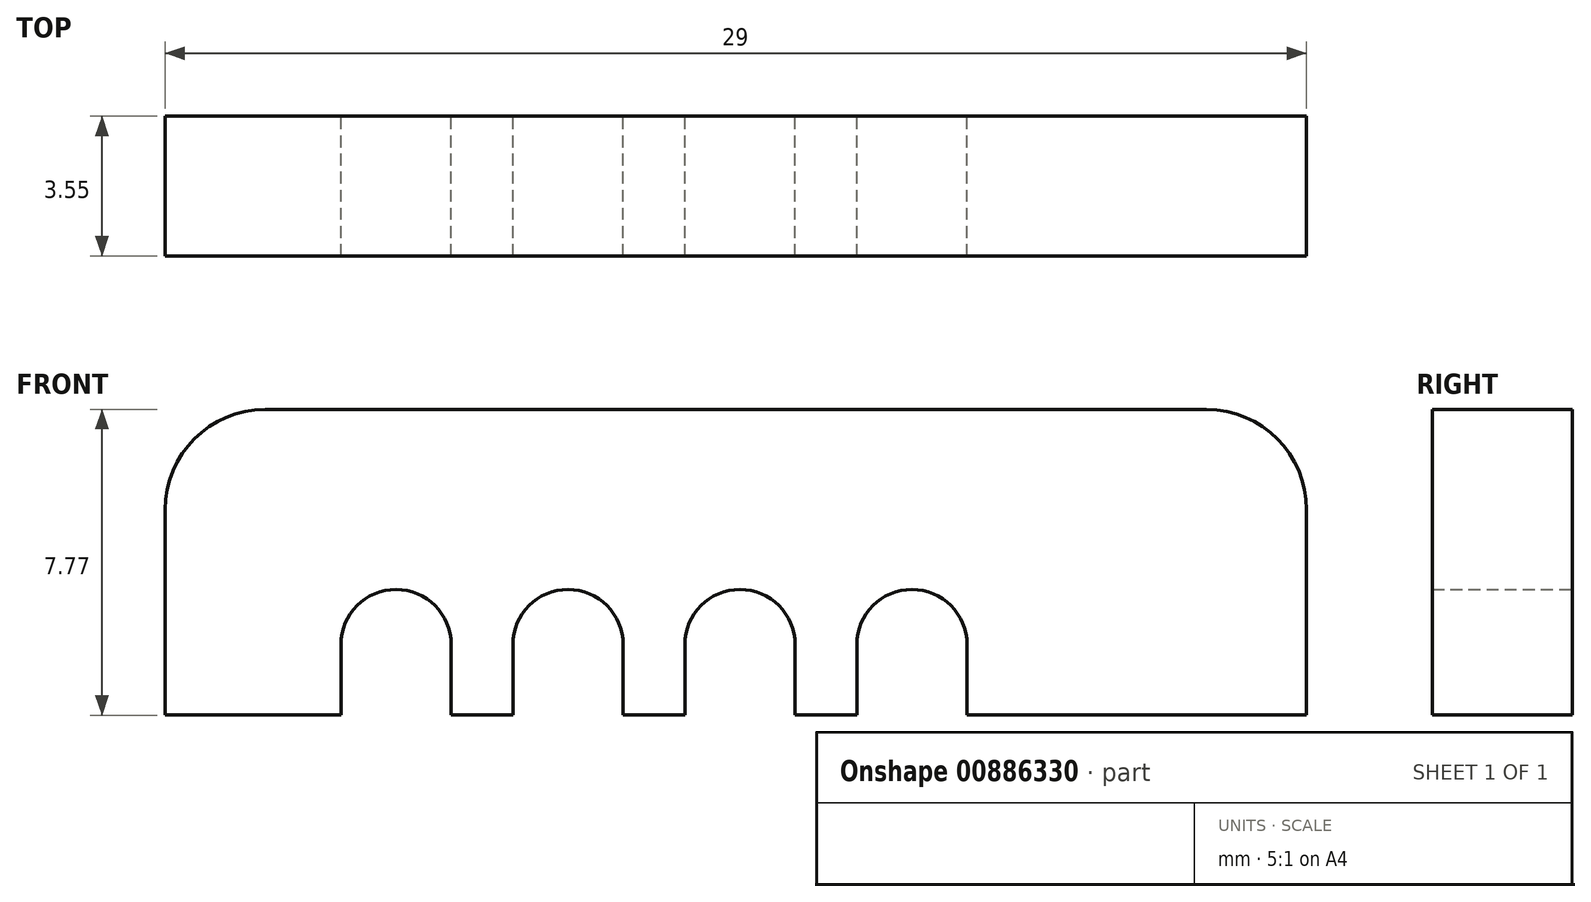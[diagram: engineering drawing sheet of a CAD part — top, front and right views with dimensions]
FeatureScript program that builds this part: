
annotation { "Feature Type Name" : "Feature", "Feature Type Description" : "" }
export const myFeature = defineFeature(function(context is Context, id is Id, definition is map)
    precondition{}
    {
        {
            var Q0;
            Q0=qCreatedBy(makeId("Front.planeOp"),FACE);
            var sketch = newSketch(context, id + "F0", { "sketchPlane" : qUnion([Q0])});
            skLineSegment(sketch, "E0.bottom", {"start": v(-13.53, 11.75) * mm, "end": v(15.47, 11.75) * mm});
            skLineSegment(sketch, "E0.top", {"start": v(-13.53, -11.75) * mm, "end": v(15.47, -11.75) * mm});
            skLineSegment(sketch, "E0.left", {"start": v(-13.53, 11.75) * mm, "end": v(-13.53, -11.75) * mm});
            skLineSegment(sketch, "E0.right", {"start": v(15.47, 11.75) * mm, "end": v(15.47, -11.75) * mm});
            skArc(sketch, "E1", {"start": v(-10.99, 11.75) * mm, "mid": v(-12.78, 11) * mm, "end": v(-13.53, 9.2) * mm});
            skArc(sketch, "E2", {"start": v(15.47, 9.2) * mm, "mid": v(14.73, 11) * mm, "end": v(12.93, 11.75) * mm});
            skArc(sketch, "E3", {"start": v(-13.53, -9.2) * mm, "mid": v(-12.78, -11) * mm, "end": v(-10.99, -11.75) * mm});
            skArc(sketch, "E4", {"start": v(12.93, -11.75) * mm, "mid": v(14.73, -11) * mm, "end": v(15.47, -9.2) * mm});
            skCircle(sketch, "E5", {"center": v(-7.66, 5.78) * mm, "radius": 1.4 * mm});
            skCircle(sketch, "E6", {"center": v(-3.29, 5.78) * mm, "radius": 1.4 * mm});
            skCircle(sketch, "E7", {"center": v(1.08, 5.78) * mm, "radius": 1.4 * mm});
            skCircle(sketch, "E8", {"center": v(5.45, 5.78) * mm, "radius": 1.4 * mm});
            skCircle(sketch, "E9", {"center": v(-5.47, 1.8) * mm, "radius": 1.4 * mm});
            skCircle(sketch, "E10", {"center": v(-1.1, 1.8) * mm, "radius": 1.4 * mm});
            skCircle(sketch, "E11", {"center": v(3.26, 1.8) * mm, "radius": 1.4 * mm});
            skCircle(sketch, "E12", {"center": v(7.63, 1.8) * mm, "radius": 1.4 * mm});
            skLineSegment(sketch, "E13.bottom", {"start": v(-14.03, 12.38) * mm, "end": v(20.56, 12.38) * mm});
            skLineSegment(sketch, "E13.top", {"start": v(-14.03, -12.38) * mm, "end": v(20.56, -12.38) * mm});
            skLineSegment(sketch, "E13.left", {"start": v(-14.03, 12.38) * mm, "end": v(-14.03, -12.38) * mm});
            skLineSegment(sketch, "E13.right", {"start": v(20.56, 12.38) * mm, "end": v(20.56, -12.38) * mm});
            skCircle(sketch, "E14", {"center": v(17.78, 0) * mm, "radius": 1.9 * mm});
            skArc(sketch, "E15", {"start": v(20.56, 9.2) * mm, "mid": v(19.63, 11.45) * mm, "end": v(17.39, 12.38) * mm});
            skArc(sketch, "E16", {"start": v(17.39, -12.38) * mm, "mid": v(19.63, -11.45) * mm, "end": v(20.56, -9.2) * mm});
            skArc(sketch, "E17", {"start": v(-14.03, -9.2) * mm, "mid": v(-13.1, -11.45) * mm, "end": v(-10.86, -12.38) * mm});
            skArc(sketch, "E18", {"start": v(-10.86, 12.38) * mm, "mid": v(-13.1, 11.45) * mm, "end": v(-14.03, 9.2) * mm});
            skLineSegment(sketch, "E19", {"start": v(-13.53, 3.98) * mm, "end": v(15.47, 3.98) * mm});
            skLineSegment(sketch, "E20", {"start": v(-13.53, 3.58) * mm, "end": v(15.47, 3.58) * mm});
            skLineSegment(sketch, "E21.bottom", {"start": v(-9.06, 5.78) * mm, "end": v(-6.26, 5.78) * mm});
            skLineSegment(sketch, "E21.top", {"start": v(-9.06, 3.98) * mm, "end": v(-6.26, 3.98) * mm});
            skLineSegment(sketch, "E21.left", {"start": v(-9.06, 5.78) * mm, "end": v(-9.06, 3.98) * mm});
            skLineSegment(sketch, "E21.right", {"start": v(-6.26, 5.78) * mm, "end": v(-6.26, 3.98) * mm});
            skLineSegment(sketch, "E22.bottom", {"start": v(-4.69, 5.78) * mm, "end": v(-1.89, 5.78) * mm});
            skLineSegment(sketch, "E22.top", {"start": v(-4.69, 3.98) * mm, "end": v(-1.89, 3.98) * mm});
            skLineSegment(sketch, "E22.left", {"start": v(-4.69, 5.78) * mm, "end": v(-4.69, 3.98) * mm});
            skLineSegment(sketch, "E22.right", {"start": v(-1.89, 5.78) * mm, "end": v(-1.89, 3.98) * mm});
            skLineSegment(sketch, "E23.bottom", {"start": v(-0.32, 5.78) * mm, "end": v(2.48, 5.78) * mm});
            skLineSegment(sketch, "E23.top", {"start": v(-0.32, 3.98) * mm, "end": v(2.48, 3.98) * mm});
            skLineSegment(sketch, "E23.left", {"start": v(-0.32, 5.78) * mm, "end": v(-0.32, 3.98) * mm});
            skLineSegment(sketch, "E23.right", {"start": v(2.48, 5.78) * mm, "end": v(2.48, 3.98) * mm});
            skLineSegment(sketch, "E24.bottom", {"start": v(4.05, 5.78) * mm, "end": v(6.85, 5.78) * mm});
            skLineSegment(sketch, "E24.top", {"start": v(4.05, 3.98) * mm, "end": v(6.85, 3.98) * mm});
            skLineSegment(sketch, "E24.left", {"start": v(4.05, 5.78) * mm, "end": v(4.05, 3.98) * mm});
            skLineSegment(sketch, "E24.right", {"start": v(6.85, 5.78) * mm, "end": v(6.85, 3.98) * mm});
            skLineSegment(sketch, "E25.bottom", {"start": v(-6.87, 3.58) * mm, "end": v(-4.07, 3.58) * mm});
            skLineSegment(sketch, "E25.top", {"start": v(-6.87, 1.8) * mm, "end": v(-4.07, 1.8) * mm});
            skLineSegment(sketch, "E25.left", {"start": v(-6.87, 3.58) * mm, "end": v(-6.87, 1.8) * mm});
            skLineSegment(sketch, "E25.right", {"start": v(-4.07, 3.58) * mm, "end": v(-4.07, 1.8) * mm});
            skLineSegment(sketch, "E26.bottom", {"start": v(-2.5, 3.58) * mm, "end": v(0.3, 3.58) * mm});
            skLineSegment(sketch, "E26.top", {"start": v(-2.5, 1.8) * mm, "end": v(0.3, 1.8) * mm});
            skLineSegment(sketch, "E26.left", {"start": v(-2.5, 3.58) * mm, "end": v(-2.5, 1.8) * mm});
            skLineSegment(sketch, "E26.right", {"start": v(0.3, 3.58) * mm, "end": v(0.3, 1.8) * mm});
            skLineSegment(sketch, "E27.bottom", {"start": v(1.86, 3.58) * mm, "end": v(4.66, 3.58) * mm});
            skLineSegment(sketch, "E27.top", {"start": v(1.86, 1.8) * mm, "end": v(4.66, 1.8) * mm});
            skLineSegment(sketch, "E27.left", {"start": v(1.86, 3.58) * mm, "end": v(1.86, 1.8) * mm});
            skLineSegment(sketch, "E27.right", {"start": v(4.66, 3.58) * mm, "end": v(4.66, 1.8) * mm});
            skLineSegment(sketch, "E28.bottom", {"start": v(6.23, 3.58) * mm, "end": v(9.03, 3.58) * mm});
            skLineSegment(sketch, "E28.top", {"start": v(6.23, 1.8) * mm, "end": v(9.03, 1.8) * mm});
            skLineSegment(sketch, "E28.left", {"start": v(6.23, 3.58) * mm, "end": v(6.23, 1.8) * mm});
            skLineSegment(sketch, "E28.right", {"start": v(9.03, 3.58) * mm, "end": v(9.03, 1.8) * mm});
            skSolve(sketch);
        }
        {
            var Q0;
            {var subQ21=sQuery(id+"F0.wireOp",EDGE,"E1");Q0=makeQuery(id+"F0.imprint","IMPRINT",FACE,{"disambiguationData":[TD([[makeQuery(id+"F0.imprint","IMPRINT",EDGE,{"derivedFrom":subQ21}),1.0]])]});}
            extrude(context, id + "F1", {"entities" : qUnion([Q0]), "depth" : 3.55 * mm, "offsetDistance" : 25 * mm});
        }
    });
